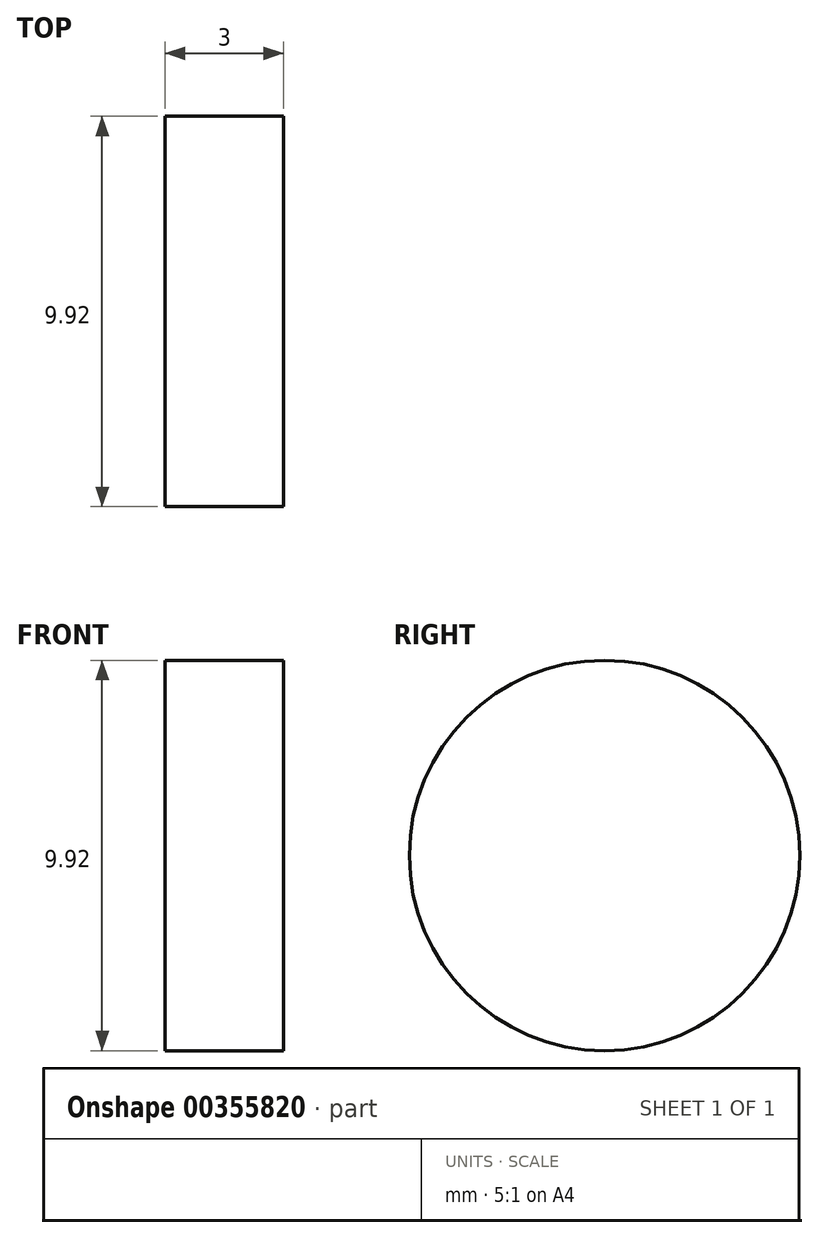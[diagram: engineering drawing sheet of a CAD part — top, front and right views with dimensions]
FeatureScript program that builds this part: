
annotation { "Feature Type Name" : "Feature", "Feature Type Description" : "" }
export const myFeature = defineFeature(function(context is Context, id is Id, definition is map)
    precondition{}
    {
        {
            var Q0;
            Q0=qCreatedBy(makeId("Right.planeOp"),FACE);
            var sketch = newSketch(context, id + "F0", { "sketchPlane" : qUnion([Q0])});
            skCircle(sketch, "E0", {"center": v(0, 0) * mm, "radius": 4.96 * mm});
            skSolve(sketch);
        }
        {
            var Q0;
            Q0 = qSketchRegion(id + "F0", true);
            extrude(context, id + "F1", {"entities" : qUnion([Q0]), "depth" : 3 * mm});
        }
    });
